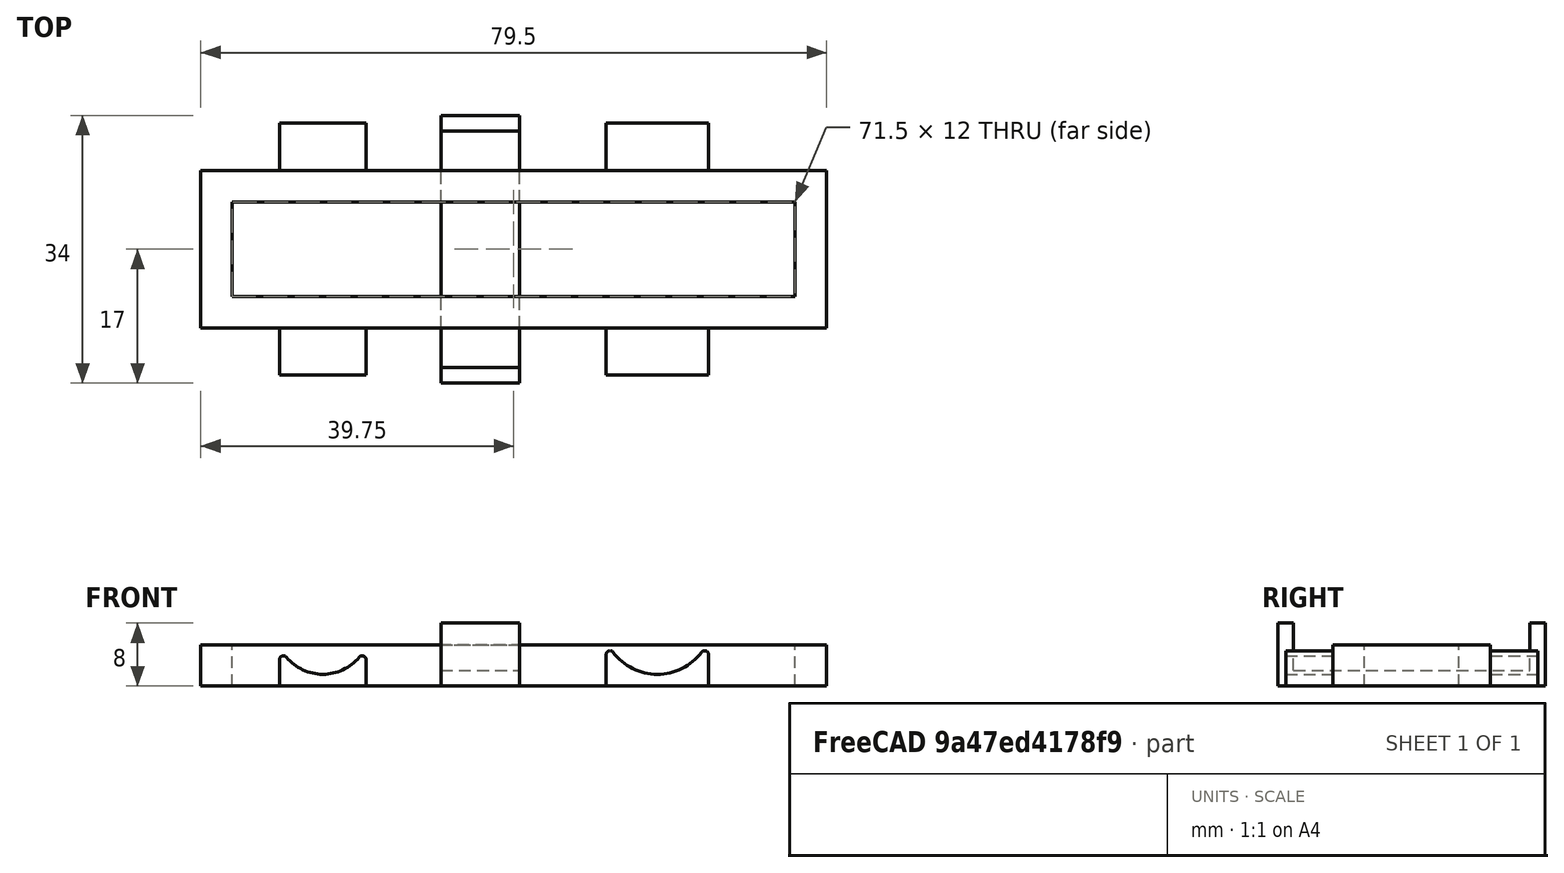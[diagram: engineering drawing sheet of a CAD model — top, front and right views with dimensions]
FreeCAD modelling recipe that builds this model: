
FCSTD DOCUMENT  (FreeCAD 0.19R24276 (Git))
Label: axleJig4
License: All rights reserved
LicenseURL: http://en.wikipedia.org/wiki/All_rights_reserved
objects: Part::Box×7, Part::Cut×5, Part::Cylinder×2, Spreadsheet::Sheet×1, Part::MultiFuse×1, Part::Fillet×1
note: 16 computed .brp shape members not serialized (recipe doc carries the construction recipe); baked Part::Feature solids carry a one-line shape summary decoded from their .brp

FEATURE [Part::Box] Box  label="Cube"
  AttacherType = Attacher::AttachEngine3D
  Height = 8
  Length = 11
  Placement = pos=(-5.5,0,0) rot=(0,0,1;0rad)
  Width = 32
  expr: Width = <<data>>.wheel_width * 2 + <<data>>.axle_width
  expr: Length = Spreadsheet.wheel_diameter_F - 1mm
  expr: .Placement.Base.x = -<<data>>.wheel_diameter_F / 2 + 0.5mm
FEATURE [Part::Box] Box008  label="base"
  AttacherType = Attacher::AttachEngine3D
  Height = 5.25
  Length = 79.5
  Placement = pos=(-15.5,6,0) rot=(0,0,1;0rad)
  Width = 20
  expr: .Placement.Base.y = <<data>>.wheel_width
  expr: Height = <<data>>.ride_height + 1.5mm
  expr: Width = <<data>>.axle_width
  expr: Length = <<data>>.wheel_diameter_F / 2 + <<data>>.wheel_base + <<data>>.wheel_diameter_R / 2 - 1mm + 25mm
  expr: .Placement.Base.x = -<<data>>.wheel_diameter_F / 2 + 0.5mm - 10mm
FEATURE [Spreadsheet::Sheet] Spreadsheet  label="data"
  cells = A4=wheel_base; B4(wheel_base)==42.5mm; A5=axle_width; B5(axle_width)==20mm; A6=ride_height; B6(ride_height)==3.75mm; A7=axle_diameter; B7(axle_diameter)==1.75mm; A8=post_wdith; B8(post_wdith)==10mm; A9=post_thickness; B9(post_thickness)==1.5mm; A10=wheel_diameter_F; B10(wheel_diameter_F)==12mm; A11=wheel_diameter_R; B11(wheel_diameter_R)==14mm; A12=wheel_width; B12(wheel_width)==6mm
FEATURE [Part::Cylinder] Cylinder
  Angle = 360
  AttacherType = Attacher::AttachEngine3D
  Height = 32
  Placement = pos=(0,0,7.5) rot=(-1,0,0;1.5708rad)
  Radius = 6
  expr: Radius = <<data>>.wheel_diameter_F / 2
  expr: Height = <<data>>.wheel_width * 2 + <<data>>.axle_width
  expr: .Placement.Base.z = <<data>>.wheel_diameter_F / 2 + 1.5mm
FEATURE [Part::Cut] Cut  label="Front Axle"
  Base = -> Box
  Tool = -> Cylinder
FEATURE [Part::Box] Box015  label="Cube015"
  AttacherType = Attacher::AttachEngine3D
  Height = 8
  Length = 13
  Placement = pos=(36,0,0) rot=(0,0,1;0rad)
  Width = 32
  expr: .Placement.Base.x = -<<data>>.wheel_diameter_R / 2 + 0.5mm + <<data>>.wheel_base
  expr: Length = Spreadsheet.wheel_diameter_R - 1mm
  expr: Width = <<data>>.wheel_width * 2 + <<data>>.axle_width
FEATURE [Part::Cylinder] Cylinder001
  Angle = 360
  AttacherType = Attacher::AttachEngine3D
  Height = 32
  Placement = pos=(42.5,0,8.5) rot=(-1,0,0;1.5708rad)
  Radius = 7
  expr: .Placement.Base.z = <<data>>.wheel_diameter_R / 2 + 1.5mm
  expr: Height = <<data>>.wheel_width * 2 + <<data>>.axle_width
  expr: Radius = <<data>>.wheel_diameter_R / 2
  expr: .Placement.Base.x = <<data>>.wheel_base
FEATURE [Part::Cut] Cut004  label="RearAxle"
  Base = -> Box015
  Tool = -> Cylinder001
FEATURE [Part::Box] Box016  label="basecutout"
  AttacherType = Attacher::AttachEngine3D
  Height = 10
  Length = 54.5
  Placement = pos=(-5.5,6,0) rot=(0,0,1;0rad)
  Width = 20
  expr: .Placement.Base.x = -<<data>>.wheel_diameter_F / 2 + 0.5mm
  expr: Length = <<data>>.wheel_diameter_F / 2 + <<data>>.wheel_base + <<data>>.wheel_diameter_R / 2 - 1mm
  expr: Width = <<data>>.axle_width
  expr: .Placement.Base.y = <<data>>.wheel_width
FEATURE [Part::MultiFuse] Fusion  label="Axles"
  Shapes = -> [Cut,Cut004]
FEATURE [Part::Cut] Cut005
  Base = -> Fusion
  Tool = -> Box016
FEATURE [Part::Box] Box017  label="basecutout001"
  AttacherType = Attacher::AttachEngine3D
  Height = 5.75
  Length = 71.5
  Placement = pos=(-11.5,10,0) rot=(0,0,1;0rad)
  Width = 12
  expr: .Placement.Base.x = -<<data>>.wheel_diameter_F / 2 + 0.5mm + 4mm - 10mm
  expr: Length = <<data>>.wheel_diameter_F / 2 + <<data>>.wheel_base + <<data>>.wheel_diameter_R / 2 - 1mm - 8mm + 25mm
  expr: Width = <<data>>.axle_width - 8mm
  expr: Height = <<data>>.ride_height + 2mm
  expr: .Placement.Base.y = <<data>>.wheel_width + 4mm
FEATURE [Part::Cut] Cut006
  Base = -> Box008
  Tool = -> Box017
FEATURE [Part::Fillet] Fillet
  Base = -> Cut005
  Edges = 8 edges r=0.5: [Edge2,Edge9,Edge14,Edge21,Edge26,Edge33,Edge38,Edge45]
FEATURE [Part::Box] Box018  label="Cube016"
  AttacherType = Attacher::AttachEngine3D
  Height = 8
  Length = 10
  Placement = pos=(15,-1,0) rot=(0,0,1;0rad)
  Width = 34
FEATURE [Part::Box] Box019  label="Cube017"
  AttacherType = Attacher::AttachEngine3D
  Height = 8
  Length = 10
  Placement = pos=(15,1,2) rot=(0,0,1;0rad)
  Width = 30
FEATURE [Part::Cut] Cut007
  Base = -> Box018
  Tool = -> Box019
